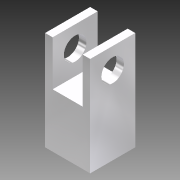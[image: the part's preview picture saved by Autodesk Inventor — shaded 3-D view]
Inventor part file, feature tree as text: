
AUTODESK INVENTOR PART (.ipt)
format: ipt  version: 2011 (Build 150239000, 239)  size: 105,984 bytes
history: native  units: in
note: dims shown in document units (in); Inventor stores cm internally (conversion verified against a paired STEP export)
features: extrude x3, sketch x3, thread x1
ambient origin geometry x8: Origin, YZ Plane, XZ Plane, XY Plane, X Axis, Y Axis, Z Axis, Center Point
bodies: Solid1 (feature_tree)
feature tree (7):
  extrude  "Extrusion1"  Depth=0.5in
  extrude  "Extrusion2"  Depth=0.125in
  extrude  "Extrusion3"  Depth=0.75in
  thread  "Thread1"  [1 undecoded]
  sketch  "Sketch1"  dims[d0=0.75in d1=0.5in]
  sketch  "Sketch2"  dims[d2=0.125in d3=0.125in]
  sketch  "Sketch3"  dims[d4=1.65in d5=0.75in d6=0.0in d7=0.75in d8=0.0in d9=0.5in d10=0.85in d11=0.0in d12=0.375in d13=0.35in d14=0.85in d15=0.0in d16=1.0in d17=0.0in]
note: 1 required parameter value undecoded (feature->parameter linkage not recoverable at this tier; creation-order binding heuristic only, values carry confidence <= 0.55)
